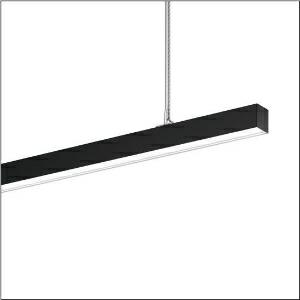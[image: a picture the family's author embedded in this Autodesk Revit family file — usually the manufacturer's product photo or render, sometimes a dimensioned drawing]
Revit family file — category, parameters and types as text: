
# Revit family: silica_r__21_51mx30tat4b_500a
name_source: partatom
category: Lighting Fixtures
units: mm (PartAtom-declared; Revit-internal decimal feet)

## family parameters
Cut with Voids When Loaded = No
Host = Face
Light Source = No
Part Type = Normal
Room Calculation Point = No
Round Connector Dimension = Use Diameter
Shared = No

## types (1)
- --- (1 x LED, 4120 lm, 33.8 W, 6500K)
    Apparent Load = 34 VA
    CIE Flux Codes = 47 79 96 58 100
    Color Rendering = 80
    Color Temperature = 6500K
    Default Elevation = 1800 mm
    Description = Silica® 21, office luminaire, primary optical cover: cover, of PMMA, opal, light emission: direct/indirect distribution, primary light characteristic: symmetric, installation type: suspended mounting, LED, rated luminous flux: 4.120lm, luminous efficacy: 116lm/W, light colour: 8tw, colour temperature: 2700..6500K, control gear: DALI DT8, with terminal, 3+2-pole, max. 2.5mm², mains connection: 220..240V, AC, 50/60Hz, rated input power: 35.5W, luminaire housing, of aluminium, matt jet black (RAL 9005), length: 1.204mm, width: 53mm, height: 53mm, protection rating (complete): IP20, insulation class (complete): insulation class I (protective earthing), certification: CE, permissible operating ambient temperature: 0..+35°C, standard: EN 50419, packaging unit: 1 piece
    Height = 53 mm
    Lamp = 1 x LED
    Lamp Light Flux = 4120 lm
    Lamp Power = 33.8 W
    Lamp count = 1
    Length = 1204 mm
    Luminous efficacy = 122 lm/W
    Manufacturer = Siteco
    ModVariant = No
    Model = 51MX30TAT4B
    Mounting Place = Ceiling
    Mounting Type = Pendant
    Number of Poles = 1
    OnlyDefault = Yes
    Power Factor = 1
    Product Name = Silica® 21
    Product group = office luminaire | ceiling pendant
    ProductGroupID = 903
    Protection Class = Protection class I
    Protection Degree = IP 20
    RLX_Detail_Level = 1
    RLX_Emergency_Light_Flux = 0 lm
    RLX_Emergency_Type = 0
    RLX_Emergency_Type_DB = No
    RlxData = <blob elided: 22861 chars, md5=26699d82>
    Socket = socket
    Standby Power = 0 W
    System Light Flux = 4120 lm
    System Power = 34 W
    Type Comments = individual setting
    Type Image = l_1335856.jpg
    URL = http://relux.com
    VarID = @adj_161117
    Voltage = 0 V
    Weight = 0.00 kg
    Width = 53 mm

## geometry (parser evidence)
native form markers: Blend x4, Sweep x11
no freeform markers — native parametric forms only
